# Revit family: LARGE SCALENE TRIANGLE (LEFT)
name_source: partatom
category: Specialty Equipment
units: mm (PartAtom-declared; Revit-internal decimal feet)

## family parameters
Always vertical = No
Cut with Voids When Loaded = No
Enable Cutting in Views = Yes
Maintain Annotation Orientation = No
OmniClass Number = 23.35.00.00
OmniClass Title = Covering, Cladding, and Finishes
Part Type = Normal
Room Calculation Point = No
Round Connector Dimension = Use Diameter
Shared = No
Work Plane-Based = Yes

## types (9) — shared parameters
Acoustics - NRC = Sound absorption varies from NRC 0.45 to 0.95 based on installation method used when tested per ASTM C423.
Assembly Code = C30
Default Elevation = 0' - 0"
Description = Acoustic Panels
Fire Rating = ASTM E84 - Class A
Manufacturer = Acoustical Surfaces, Inc.
Material = Envirocoustic Wood Wool
Model = Envirocoustic Wood Wool
Recycled Content Percentage = 0%
Type Comments = Acoustic Panels
URL = https://www.acousticalsurfaces.com

## per-type parameters (varying)
| type | Finish | Thickness |
| 1-3/8 inch thick Primed White | Paint - Acoustical-Surfaces - Primed White | 0' - 1 1/2" |
| 1-3/8 inch thick Primed Clear | Paint - Acoustical-Surfaces - Primed Clear | 0' - 1 1/2" |
| 1-3/8 inch thick Custom Painted | Paint - Acoustical-Surfaces - Custom Painted | 0' - 1 1/2" |
| 2 inch thick Primed White | Paint - Acoustical-Surfaces - Primed White | 0' - 2" |
| 2 inch thick Primed Clear | Paint - Acoustical-Surfaces - Primed Clear | 0' - 2" |
| 2 inch thick Custom Painted | Paint - Acoustical-Surfaces - Custom Painted | 0' - 2" |
| 1 inch thick Primed White | Paint - Acoustical-Surfaces - Primed White | 0' - 1" |
| 1 inch thick Primed Clear | Paint - Acoustical-Surfaces - Primed Clear | 0' - 1" |
| 1 inch thick Custom Painted | Paint - Acoustical-Surfaces - Custom Painted | 0' - 1" |

## geometry (parser evidence)
native form markers: Sweep x3
no freeform markers — native parametric forms only
